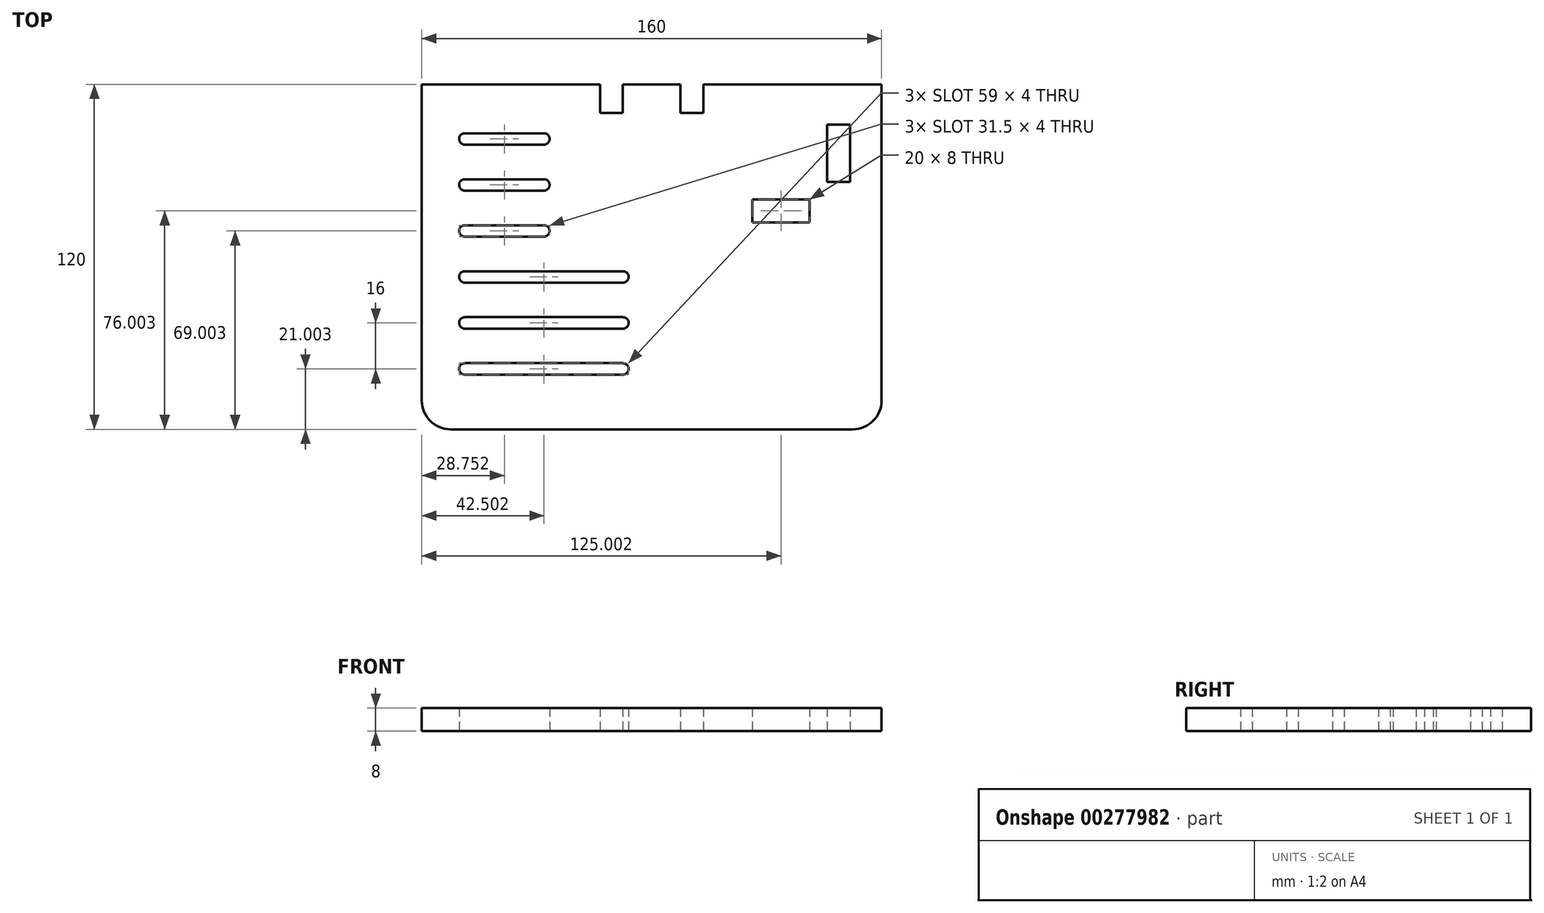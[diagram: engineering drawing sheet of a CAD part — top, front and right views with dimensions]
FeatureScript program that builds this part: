
annotation { "Feature Type Name" : "Feature", "Feature Type Description" : "" }
export const myFeature = defineFeature(function(context is Context, id is Id, definition is map)
    precondition{}
    {
        {
            var Q0;
            Q0=qCreatedBy(makeId("Top.planeOp"),FACE);
            var sketch = newSketch(context, id + "F0", { "sketchPlane" : qUnion([Q0])});
            skLineSegment(sketch, "E0", {"start": v(-45.56, -13.54) * mm, "end": v(16.44, -13.54) * mm});
            skLineSegment(sketch, "E1", {"start": v(16.44, -13.54) * mm, "end": v(16.44, -23.54) * mm});
            skLineSegment(sketch, "E2", {"start": v(16.44, -23.54) * mm, "end": v(24.44, -23.54) * mm});
            skLineSegment(sketch, "E3", {"start": v(24.44, -23.54) * mm, "end": v(24.44, -13.54) * mm});
            skLineSegment(sketch, "E4", {"start": v(24.44, -13.54) * mm, "end": v(44.44, -13.54) * mm});
            skLineSegment(sketch, "E5", {"start": v(44.44, -13.54) * mm, "end": v(44.44, -23.54) * mm});
            skLineSegment(sketch, "E6", {"start": v(44.44, -23.54) * mm, "end": v(52.44, -23.54) * mm});
            skLineSegment(sketch, "E7", {"start": v(52.44, -23.54) * mm, "end": v(52.44, -13.54) * mm});
            skLineSegment(sketch, "E8", {"start": v(114.44, -13.54) * mm, "end": v(114.44, -133.54) * mm});
            skLineSegment(sketch, "E9", {"start": v(114.44, -133.54) * mm, "end": v(-45.56, -133.54) * mm});
            skLineSegment(sketch, "E10", {"start": v(-45.56, -133.54) * mm, "end": v(-45.56, -13.54) * mm});
            skLineSegment(sketch, "E11", {"start": v(52.44, -13.54) * mm, "end": v(114.44, -13.54) * mm});
            skLineSegment(sketch, "E12.0", {"start": v(-30.56, -80.54) * mm, "end": v(24.44, -80.54) * mm});
            skArc(sketch, "E13.3.startCap", {"start": v(-30.56, -82.54) * mm, "mid": v(-32.56, -80.54) * mm, "end": v(-30.56, -78.54) * mm});
            skArc(sketch, "E13.3.endCap", {"start": v(24.44, -78.54) * mm, "mid": v(26.44, -80.54) * mm, "end": v(24.44, -82.54) * mm});
            skLineSegment(sketch, "E13.3.left", {"start": v(-30.56, -78.54) * mm, "end": v(24.44, -78.54) * mm});
            skLineSegment(sketch, "E13.3.right", {"start": v(-30.56, -82.54) * mm, "end": v(24.44, -82.54) * mm});
            skLineSegment(sketch, "E14.0.1.0", {"start": v(-30.56, -94.54) * mm, "end": v(24.44, -94.54) * mm});
            skLineSegment(sketch, "E14.0.1.1", {"start": v(-30.56, -96.54) * mm, "end": v(24.44, -96.54) * mm});
            skLineSegment(sketch, "E14.0.1.2", {"start": v(-30.56, -98.54) * mm, "end": v(24.44, -98.54) * mm});
            skArc(sketch, "E14.0.1.3", {"start": v(-30.56, -98.54) * mm, "mid": v(-32.56, -96.54) * mm, "end": v(-30.56, -94.54) * mm});
            skArc(sketch, "E14.0.1.4", {"start": v(24.44, -94.54) * mm, "mid": v(26.44, -96.54) * mm, "end": v(24.44, -98.54) * mm});
            skLineSegment(sketch, "E14.direction1", {"start": v(-30.56, -82.54) * mm, "end": v(-5.56, -82.54) * mm, "construction": true});
            skLineSegment(sketch, "E14.direction2", {"start": v(-30.56, -82.54) * mm, "end": v(-30.56, -98.54) * mm, "construction": true});
            skLineSegment(sketch, "E15.0.0.2", {"start": v(-30.56, -110.54) * mm, "end": v(24.44, -110.54) * mm});
            skLineSegment(sketch, "E15.3.0.2", {"start": v(-30.56, -112.54) * mm, "end": v(24.44, -112.54) * mm});
            skLineSegment(sketch, "E15.6.0.2", {"start": v(-30.56, -114.54) * mm, "end": v(24.44, -114.54) * mm});
            skArc(sketch, "E15.9.0.2", {"start": v(-30.56, -114.54) * mm, "mid": v(-32.56, -112.54) * mm, "end": v(-30.56, -110.54) * mm});
            skArc(sketch, "E15.13.0.2", {"start": v(24.44, -110.54) * mm, "mid": v(26.44, -112.54) * mm, "end": v(24.44, -114.54) * mm});
            skLineSegment(sketch, "E16", {"start": v(-30.56, -48.54) * mm, "end": v(-3.06, -48.54) * mm});
            skLineSegment(sketch, "E17", {"start": v(-30.56, -64.54) * mm, "end": v(-3.06, -64.54) * mm});
            skArc(sketch, "E18.0.startCap", {"start": v(-30.56, -50.54) * mm, "mid": v(-32.56, -48.54) * mm, "end": v(-30.56, -46.54) * mm});
            skArc(sketch, "E18.0.endCap", {"start": v(-3.06, -46.54) * mm, "mid": v(-1.06, -48.54) * mm, "end": v(-3.06, -50.54) * mm});
            skLineSegment(sketch, "E18.0.left", {"start": v(-30.56, -46.54) * mm, "end": v(-3.06, -46.54) * mm});
            skLineSegment(sketch, "E18.0.right", {"start": v(-30.56, -50.54) * mm, "end": v(-3.06, -50.54) * mm});
            skArc(sketch, "E19.0.startCap", {"start": v(-30.56, -66.54) * mm, "mid": v(-32.56, -64.54) * mm, "end": v(-30.56, -62.54) * mm});
            skArc(sketch, "E19.0.endCap", {"start": v(-3.06, -62.54) * mm, "mid": v(-1.06, -64.54) * mm, "end": v(-3.06, -66.54) * mm});
            skLineSegment(sketch, "E19.0.left", {"start": v(-30.56, -62.54) * mm, "end": v(-3.06, -62.54) * mm});
            skLineSegment(sketch, "E19.0.right", {"start": v(-30.56, -66.54) * mm, "end": v(-3.06, -66.54) * mm});
            skLineSegment(sketch, "E20", {"start": v(-30.56, -32.54) * mm, "end": v(-3.06, -32.54) * mm});
            skArc(sketch, "E21.0.startCap", {"start": v(-30.56, -34.54) * mm, "mid": v(-32.56, -32.54) * mm, "end": v(-30.56, -30.54) * mm});
            skArc(sketch, "E21.0.endCap", {"start": v(-3.06, -30.54) * mm, "mid": v(-1.06, -32.54) * mm, "end": v(-3.06, -34.54) * mm});
            skLineSegment(sketch, "E21.0.left", {"start": v(-30.56, -30.54) * mm, "end": v(-3.06, -30.54) * mm});
            skLineSegment(sketch, "E21.0.right", {"start": v(-30.56, -34.54) * mm, "end": v(-3.06, -34.54) * mm});
            skLineSegment(sketch, "E22.0", {"start": v(89.44, -53.54) * mm, "end": v(69.44, -53.54) * mm});
            skLineSegment(sketch, "E23.0", {"start": v(89.44, -61.54) * mm, "end": v(69.44, -61.54) * mm});
            skLineSegment(sketch, "E24.0", {"start": v(95.44, -27.54) * mm, "end": v(95.44, -47.54) * mm});
            skLineSegment(sketch, "E25.0", {"start": v(103.44, -27.54) * mm, "end": v(103.44, -47.54) * mm});
            skLineSegment(sketch, "E26", {"start": v(89.44, -53.54) * mm, "end": v(89.44, -61.54) * mm});
            skLineSegment(sketch, "E27", {"start": v(69.44, -53.54) * mm, "end": v(69.44, -61.54) * mm});
            skLineSegment(sketch, "E28", {"start": v(95.44, -47.54) * mm, "end": v(103.44, -47.54) * mm});
            skLineSegment(sketch, "E29", {"start": v(103.44, -27.54) * mm, "end": v(95.44, -27.54) * mm});
            skSolve(sketch);
        }
        {
            var Q0;
            Q0=qSketchRegion(id+"F0",true);
            extrude(context, id + "F1", {"entities" : qUnion([Q0]), "depth" : 8 * mm});
        }
        {
            var Q0;
            Q0=makeQuery(id+"F1.opExtrude","SWEPT_EDGE",EDGE,{"disambiguationData":[OSD([sQuery(id+"F0.wireOp",EDGE,"E9"),sQuery(id+"F0.wireOp",EDGE,"E10")])]});
            var Q1;
            Q1=makeQuery(id+"F1.opExtrude","SWEPT_EDGE",EDGE,{"disambiguationData":[OSD([sQuery(id+"F0.wireOp",EDGE,"E8"),sQuery(id+"F0.wireOp",EDGE,"E9")])]});
            fillet(context, id + "F2", {"entities" : qUnion([Q0, Q1]), "radius" : 10 * mm, "tangentPropagation" : true, "allowEdgeOverflow" : false});
        }
    });
